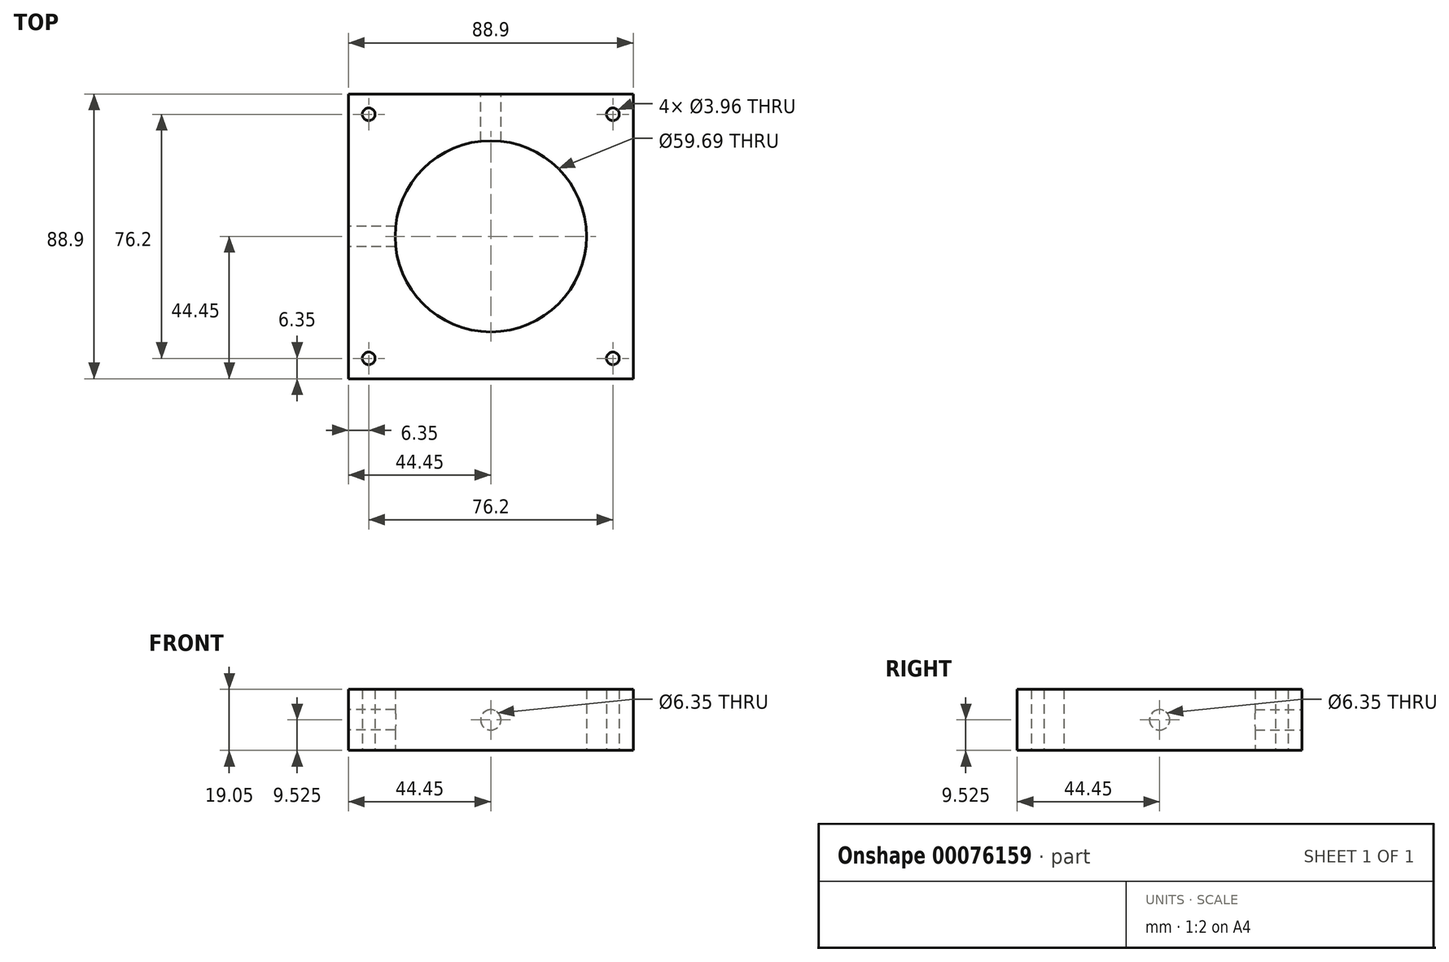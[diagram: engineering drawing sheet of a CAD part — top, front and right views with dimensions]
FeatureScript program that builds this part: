
annotation { "Feature Type Name" : "Feature", "Feature Type Description" : "" }
export const myFeature = defineFeature(function(context is Context, id is Id, definition is map)
    precondition{}
    {
        {
            var Q0;
            Q0=qCreatedBy(makeId("Top.planeOp"),FACE);
            var sketch = newSketch(context, id + "F0", { "sketchPlane" : qUnion([Q0])});
            skLineSegment(sketch, "E0.bottom", {"start": v(44.45, 44.45) * mm, "end": v(-44.45, 44.45) * mm});
            skLineSegment(sketch, "E0.top", {"start": v(44.45, -44.45) * mm, "end": v(-44.45, -44.45) * mm});
            skLineSegment(sketch, "E0.left", {"start": v(44.45, 44.45) * mm, "end": v(44.45, -44.45) * mm});
            skLineSegment(sketch, "E0.right", {"start": v(-44.45, 44.45) * mm, "end": v(-44.45, -44.45) * mm});
            skPoint(sketch, "E0.middle", {"position": v(0, 0) * mm});
            skCircle(sketch, "E1", {"center": v(0, 0) * mm, "radius": 29.85 * mm});
            skCircle(sketch, "E2", {"center": v(-38.1, 38.1) * mm, "radius": 1.98 * mm});
            skCircle(sketch, "E3", {"center": v(38.1, 38.1) * mm, "radius": 1.98 * mm});
            skCircle(sketch, "E4", {"center": v(38.1, -38.1) * mm, "radius": 1.98 * mm});
            skCircle(sketch, "E5", {"center": v(-38.1, -38.1) * mm, "radius": 1.98 * mm});
            skSolve(sketch);
        }
        {
            var Q0;
            Q0 = qSketchRegion(id + "F0", true);
            extrude(context, id + "F1", {"entities" : qUnion([Q0]), "depth" : 19.05 * mm});
        }
        {
            var Q0;
            Q0=makeQuery(id+"F1.opExtrude","SWEPT_FACE",FACE,{"disambiguationData":[OSD([sQuery(id+"F0.wireOp",EDGE,"E0.bottom")])]});
            var sketch = newSketch(context, id + "F2", { "sketchPlane" : qUnion([Q0])});
            skCircle(sketch, "E6", {"center": v(0, 9.53) * mm, "radius": 3.18 * mm});
            skPoint(sketch, "E6.centerSnap0", {"position": v(44.45, 9.53) * mm});
            skSolve(sketch);
        }
        {
            var Q0;
            Q0 = qSketchRegion(id + "F2", true);
            extrude(context, id + "F3", {"entities" : qUnion([Q0]), "operationType" : NewBodyOperationType.REMOVE, "oppositeDirection" : true, "depth" : 25.4 * mm});
        }
        {
            var Q0;
            Q0=makeQuery(id+"F1.opExtrude","SWEPT_FACE",FACE,{"disambiguationData":[OSD([sQuery(id+"F0.wireOp",EDGE,"E0.right")])]});
            var sketch = newSketch(context, id + "F4", { "sketchPlane" : qUnion([Q0])});
            skCircle(sketch, "E7", {"center": v(0, 9.53) * mm, "radius": 3.18 * mm});
            skPoint(sketch, "E7.centerSnap0", {"position": v(44.45, 9.53) * mm});
            skSolve(sketch);
        }
        {
            var Q0;
            Q0 = qSketchRegion(id + "F4", true);
            extrude(context, id + "F5", {"entities" : qUnion([Q0]), "operationType" : NewBodyOperationType.REMOVE, "oppositeDirection" : true, "depth" : 25.4 * mm});
        }
    });
